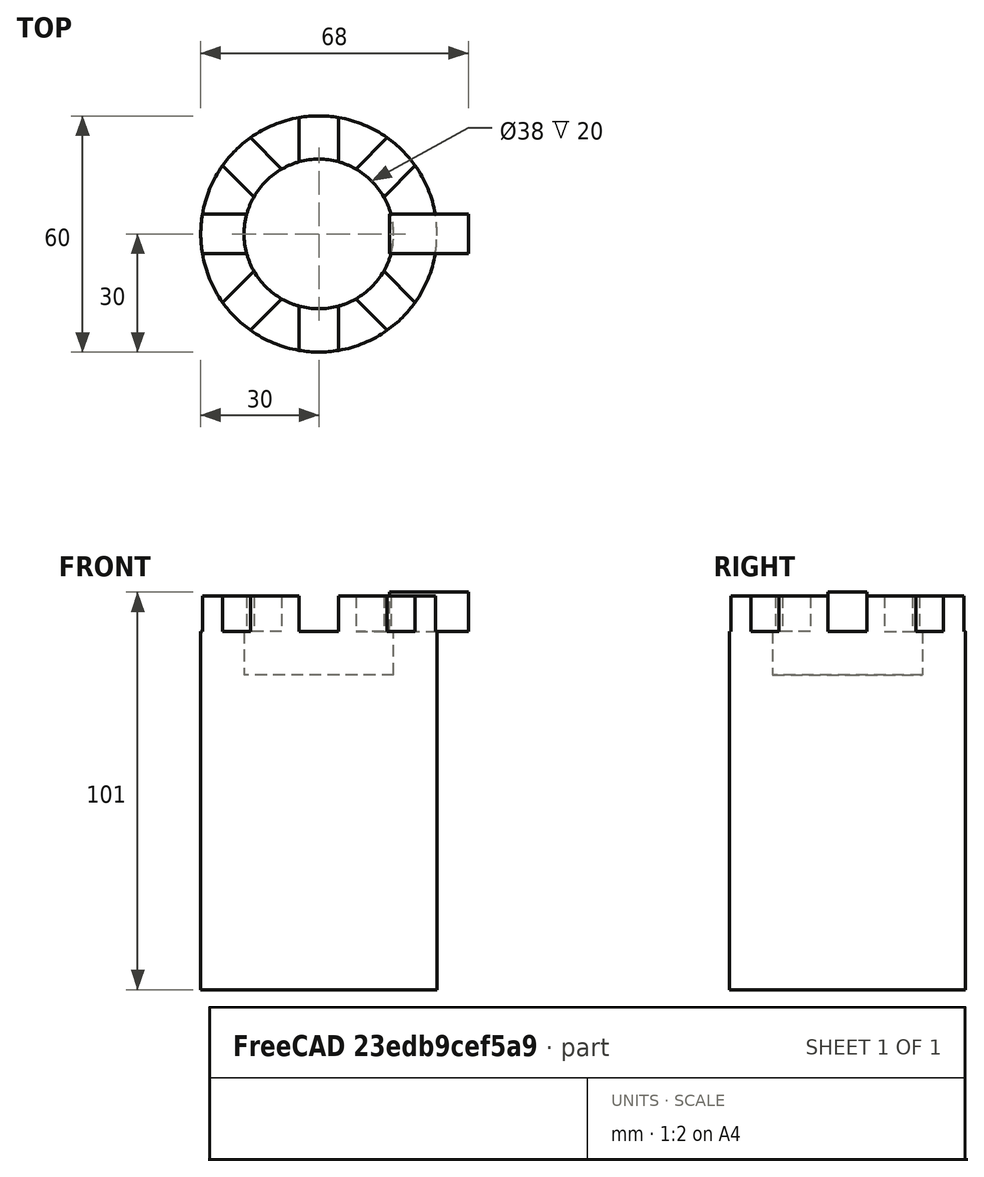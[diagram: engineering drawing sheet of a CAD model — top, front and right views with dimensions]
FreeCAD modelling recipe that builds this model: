
FCSTD DOCUMENT  (FreeCAD 1.0R39319 (Git))
Label: ojt1_t11r03_tower
License: All rights reserved
LicenseURL: https://en.wikipedia.org/wiki/All_rights_reserved
objects: Part::Cylinder×2, Part::Cut×2, Part::Box×1, Part::FeaturePython×1
note: 5 computed .brp shape members not serialized (recipe doc carries the construction recipe); baked Part::Feature solids carry a one-line shape summary decoded from their .brp

FEATURE [Part::Cylinder] Cylinder  label="Cilindre"
  Angle = 360
  AttacherType = Attacher::AttachEngine3D
  FirstAngle = 0
  Height = 100
  Radius = 30
  SecondAngle = 0
FEATURE [Part::Box] Box  label="Cub"
  AttacherType = Attacher::AttachEngine3D
  Height = 10
  Length = 20
  Placement = pos=(18,-5,91) rot=(0,0,1;0rad)
  Width = 10
FEATURE [Part::FeaturePython] Array  # Draft array (typed FeaturePython)
  AlwaysSyncPlacement = false
  Angle = 360
  ArrayType = 1
  Axis = (0,0,1)
  Base = -> Box
  Center = (0,0,0)
  Count = 8
  ExpandArray = false
  Fuse = false
  IntervalAxis = (0,0,0)
  IntervalX = (50,0,0)
  IntervalY = (0,50,0)
  IntervalZ = (0,0,50)
  NumberCircles = 3
  NumberPolar = 8
  NumberX = 2
  NumberY = 2
  NumberZ = 1
  PlacementList = 8 placements: [(18,-5,91),(16.2635,9.19239,91),(5,18,91),(-9.19239,16.2635,91),(-18,5,91),(-16.2635,-9.19239,91),(-5,-18,91),(9.19239,-16.2635,91)]
  RadialDistance = 50
  ScaleList = (8) [(1,1,1),(1,1,1),(1,1,1),(1,1,1),(1,1,1),(1,1,1),(1,1,1),(1,1,1)]
  Symmetry = 1
  TangentialDistance = 25
FEATURE [Part::Cut] Cut
  Base = -> Cylinder
  Refine = true
  Tool = -> Array
FEATURE [Part::Cylinder] Cylinder001  label="Cilindre001"
  Angle = 360
  AttacherType = Attacher::AttachEngine3D
  FirstAngle = 0
  Height = 20
  Placement = pos=(0,0,80) rot=(0,0,1;0rad)
  Radius = 19
  SecondAngle = 0
FEATURE [Part::Cut] Cut001
  Base = -> Cut
  Refine = true
  Tool = -> Cylinder001
